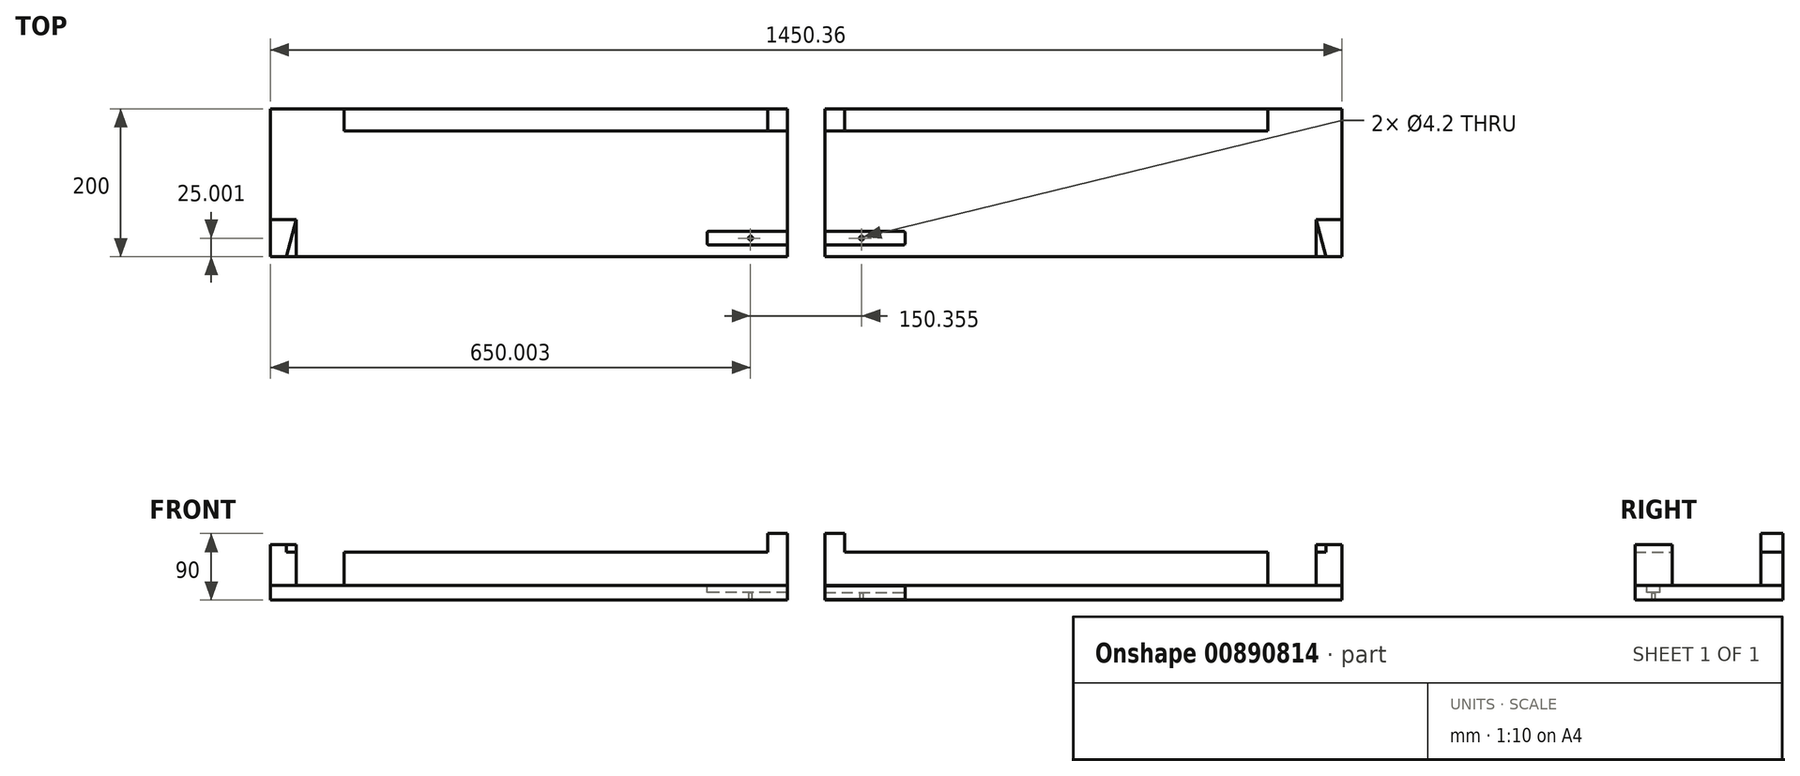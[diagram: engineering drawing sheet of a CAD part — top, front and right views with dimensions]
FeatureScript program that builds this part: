
annotation { "Feature Type Name" : "Feature", "Feature Type Description" : "" }
export const myFeature = defineFeature(function(context is Context, id is Id, definition is map)
    precondition{}
    {
        {
            var Q0;
            Q0=qCreatedBy(makeId("Top.planeOp"),FACE);
            var sketch = newSketch(context, id + "F0", { "sketchPlane" : qUnion([Q0])});
            skLineSegment(sketch, "E0.bottom", {"start": v(-675.18, 188.43) * mm, "end": v(54.82, 188.43) * mm});
            skLineSegment(sketch, "E0.top", {"start": v(-675.18, -11.57) * mm, "end": v(54.82, -11.57) * mm});
            skLineSegment(sketch, "E0.left", {"start": v(-675.18, 188.43) * mm, "end": v(-675.18, -11.57) * mm});
            skLineSegment(sketch, "E0.right", {"start": v(54.82, 188.43) * mm, "end": v(54.82, -11.57) * mm});
            skSolve(sketch);
        }
        {
            var Q0;
            Q0=makeQuery(id+"F0.imprint","IMPRINT",FACE,{"disambiguationData":[TD([[makeQuery(id+"F0.imprint","IMPRINT",EDGE,{"derivedFrom":sQuery(id+"F0.wireOp",EDGE,"E0.bottom")}),-1.0]])]});
            extrude(context, id + "F1", {"entities" : qUnion([Q0]), "depth" : 20 * mm, "offsetDistance" : 25 * mm});
        }
        {
            var Q0;
            Q0=makeQuery(id+"F1.opExtrude","CAP_FACE",FACE,{"disambiguationData":[OSD([sQuery(id+"F0.wireOp",EDGE,"E0.bottom"),sQuery(id+"F0.wireOp",EDGE,"E0.top"),sQuery(id+"F0.wireOp",EDGE,"E0.left"),sQuery(id+"F0.wireOp",EDGE,"E0.right")])],"isStart":false});
            var sketch = newSketch(context, id + "F2", { "sketchPlane" : qUnion([Q0])});
            skLineSegment(sketch, "E1.bottom", {"start": v(54.82, 188.43) * mm, "end": v(-545.18, 188.43) * mm});
            skLineSegment(sketch, "E1.top", {"start": v(54.82, 158.43) * mm, "end": v(-545.18, 158.43) * mm});
            skLineSegment(sketch, "E1.left", {"start": v(54.82, 188.43) * mm, "end": v(54.82, 158.43) * mm});
            skLineSegment(sketch, "E1.right", {"start": v(-545.18, 188.43) * mm, "end": v(-545.18, 158.43) * mm});
            skSolve(sketch);
        }
        {
            var Q0;
            Q0=makeQuery(id+"F2.imprint","IMPRINT",FACE,{"disambiguationData":[TD([[makeQuery(id+"F2.imprint","IMPRINT",EDGE,{"derivedFrom":sQuery(id+"F2.wireOp",EDGE,"E1.bottom")}),-1.0]])]});
            extrude(context, id + "F3", {"entities" : qUnion([Q0]), "depth" : 45 * mm, "offsetDistance" : 25 * mm});
        }
        {
            var Q0;
            Q0=makeQuery(id+"F3.opExtrude","CAP_FACE",FACE,{"disambiguationData":[OSD([sQuery(id+"F2.wireOp",EDGE,"E1.bottom"),sQuery(id+"F2.wireOp",EDGE,"E1.top"),sQuery(id+"F2.wireOp",EDGE,"E1.left"),sQuery(id+"F2.wireOp",EDGE,"E1.right")])],"isStart":false});
            var sketch = newSketch(context, id + "F4", { "sketchPlane" : qUnion([Q0])});
            skLineSegment(sketch, "E2.bottom", {"start": v(54.82, 188.43) * mm, "end": v(27.82, 188.43) * mm});
            skLineSegment(sketch, "E2.top", {"start": v(54.82, 158.43) * mm, "end": v(27.82, 158.43) * mm});
            skLineSegment(sketch, "E2.left", {"start": v(54.82, 188.43) * mm, "end": v(54.82, 158.43) * mm});
            skLineSegment(sketch, "E2.right", {"start": v(27.82, 188.43) * mm, "end": v(27.82, 158.43) * mm});
            skSolve(sketch);
        }
        {
            var Q0;
            Q0=makeQuery(id+"F4.imprint","IMPRINT",FACE,{"disambiguationData":[TD([[makeQuery(id+"F4.imprint","IMPRINT",EDGE,{"derivedFrom":sQuery(id+"F4.wireOp",EDGE,"E2.bottom")}),-1.0]])]});
            extrude(context, id + "F5", {"entities" : qUnion([Q0]), "operationType" : NewBodyOperationType.ADD, "depth" : 25 * mm, "offsetDistance" : 25 * mm});
        }
        {
            var Q0;
            Q0=makeQuery(id+"F1.opExtrude","CAP_FACE",FACE,{"disambiguationData":[OSD([sQuery(id+"F0.wireOp",EDGE,"E0.bottom"),sQuery(id+"F0.wireOp",EDGE,"E0.top"),sQuery(id+"F0.wireOp",EDGE,"E0.left"),sQuery(id+"F0.wireOp",EDGE,"E0.right")])],"isStart":false});
            var sketch = newSketch(context, id + "F6", { "sketchPlane" : qUnion([Q0])});
            skLineSegment(sketch, "E3.bottom", {"start": v(-665.18, -11.57) * mm, "end": v(-610.48, -11.57) * mm});
            skLineSegment(sketch, "E3.top", {"start": v(-665.18, 38.43) * mm, "end": v(-610.48, 38.43) * mm});
            skLineSegment(sketch, "E3.right", {"start": v(-610.48, -11.57) * mm, "end": v(-610.48, 38.43) * mm});
            skLineSegment(sketch, "E4.0", {"start": v(-665.18, -11.57) * mm, "end": v(-665.18, 38.43) * mm});
            skSolve(sketch);
        }
        {
            var Q0;
            Q0=makeQuery(id+"F6.imprint","IMPRINT",FACE,{"disambiguationData":[TD([[makeQuery(id+"F6.imprint","IMPRINT",EDGE,{"derivedFrom":sQuery(id+"F6.wireOp",EDGE,"E3.bottom")}),1.0]])]});
            extrude(context, id + "F7", {"entities" : qUnion([Q0]), "depth" : 45 * mm, "offsetDistance" : 25 * mm});
        }
        {
            var Q0;
            Q0=makeQuery(id+"F7.opExtrude","CAP_FACE",FACE,{"disambiguationData":[OSD([sQuery(id+"F6.wireOp",EDGE,"E3.bottom"),sQuery(id+"F6.wireOp",EDGE,"E3.top"),sQuery(id+"F6.wireOp",EDGE,"E3.left"),sQuery(id+"F6.wireOp",EDGE,"E3.right")])],"isStart":false});
            var sketch = newSketch(context, id + "F8", { "sketchPlane" : qUnion([Q0])});
            skLineSegment(sketch, "E5", {"start": v(-665.18, 38.43) * mm, "end": v(-610.48, 38.43) * mm});
            skLineSegment(sketch, "E6", {"start": v(-665.18, -11.57) * mm, "end": v(-665.18, 38.43) * mm});
            skLineSegment(sketch, "E7", {"start": v(-665.18, -11.57) * mm, "end": v(-623.58, -11.57) * mm});
            skLineSegment(sketch, "E8", {"start": v(-610.48, 38.43) * mm, "end": v(-623.58, -11.57) * mm});
            skSolve(sketch);
        }
        {
            var Q0;
            Q0=makeQuery(id+"F8.imprint","IMPRINT",FACE,{"disambiguationData":[TD([[makeQuery(id+"F8.imprint","IMPRINT",EDGE,{"derivedFrom":sQuery(id+"F8.wireOp",EDGE,"E5")}),-1.0]])]});
            extrude(context, id + "F9", {"entities" : qUnion([Q0]), "operationType" : NewBodyOperationType.ADD, "depth" : 10 * mm, "offsetDistance" : 25 * mm});
        }
        {
            var Q0;
            Q0=makeQuery(id+"F1.opExtrude","CAP_FACE",FACE,{"disambiguationData":[OSD([sQuery(id+"F0.wireOp",EDGE,"E0.bottom"),sQuery(id+"F0.wireOp",EDGE,"E0.top"),sQuery(id+"F0.wireOp",EDGE,"E0.left"),sQuery(id+"F0.wireOp",EDGE,"E0.right")])],"isStart":false});
            var sketch = newSketch(context, id + "F10", { "sketchPlane" : qUnion([Q0])});
            skLineSegment(sketch, "E9", {"start": v(54.82, 13.43) * mm, "end": v(-82.04, 13.43) * mm, "construction": true});
            skLineSegment(sketch, "E10.0", {"start": v(57.24, 22.43) * mm, "end": v(-52.18, 22.43) * mm});
            skLineSegment(sketch, "E11.0", {"start": v(57.24, 4.43) * mm, "end": v(-52.18, 4.43) * mm});
            skLineSegment(sketch, "E12", {"start": v(57.24, 22.43) * mm, "end": v(57.24, 4.43) * mm});
            skLineSegment(sketch, "E13", {"start": v(-54.18, 20.43) * mm, "end": v(-54.18, 6.43) * mm});
            skPoint(sketch, "E14.visualSharp", {"position": v(-54.18, 22.43) * mm});
            skArc(sketch, "E14.filletArc", {"start": v(-52.18, 22.43) * mm, "mid": v(-53.6, 21.84) * mm, "end": v(-54.18, 20.43) * mm});
            skPoint(sketch, "E15.visualSharp", {"position": v(-54.18, 4.43) * mm});
            skArc(sketch, "E15.filletArc", {"start": v(-54.18, 6.43) * mm, "mid": v(-53.6, 5.02) * mm, "end": v(-52.18, 4.43) * mm});
            skSolve(sketch);
        }
        {
            var Q0;
            Q0=makeQuery(id+"F10.imprint","IMPRINT",FACE,{"disambiguationData":[TD([[makeQuery(id+"F10.imprint","IMPRINT",EDGE,{"derivedFrom":sQuery(id+"F10.wireOp",EDGE,"E13")}),1.0]])]});
            extrude(context, id + "F11", {"entities" : qUnion([Q0]), "operationType" : NewBodyOperationType.REMOVE, "oppositeDirection" : true, "depth" : 10 * mm, "offsetDistance" : 25 * mm});
        }
        {
            var Q0;
            Q0=makeQuery(id+"F11.boolean.opBoolean","COPY",FACE,{"derivedFrom":makeQuery(id+"F11.opExtrude","CAP_FACE",FACE,{"disambiguationData":[OSD([sQuery(id+"F0.wireOp",EDGE,"E0.right"),sQuery(id+"F10.wireOp",EDGE,"E10.0"),sQuery(id+"F10.wireOp",EDGE,"E11.0"),sQuery(id+"F10.wireOp",EDGE,"E13"),sQuery(id+"F10.wireOp",EDGE,"E14.filletArc"),sQuery(id+"F10.wireOp",EDGE,"E15.filletArc")])],"isStart":false})});
            var sketch = newSketch(context, id + "F12", { "sketchPlane" : qUnion([Q0])});
            skLineSegment(sketch, "E16", {"start": v(-59.39, 13.43) * mm, "end": v(59.1, 13.43) * mm, "construction": true});
            skLineSegment(sketch, "E17", {"start": v(4.82, 22.43) * mm, "end": v(4.82, 4.43) * mm, "construction": true});
            skPoint(sketch, "E18", {"position": v(4.82, 13.43) * mm});
            skSolve(sketch);
        }
        {
            var Q0;
            Q0=sQuery(id+"F12.wireOp",VERTEX,"E18");
            var Q1;
            Q1=makeQuery(id+"F1.opExtrude","SWEPT_BODY",BODY,{"disambiguationData":[OSD([sQuery(id+"F0.wireOp",EDGE,"E0.bottom"),sQuery(id+"F0.wireOp",EDGE,"E0.top"),sQuery(id+"F0.wireOp",EDGE,"E0.left"),sQuery(id+"F0.wireOp",EDGE,"E0.right")])]});
            hole(context, id + "F13", {"style" : HoleStyle.C_SINK, "endStyle" : HoleEndStyle.THROUGH, "holeDiameter" : 4.2 * mm, "cSinkDiameter" : 5.5 * mm, "cSinkAngle" : 90 * degree, "majorDiameter" : 5 * mm, "isTappedThrough" : true, "tappedDepth" : 12 * mm, "tapClearance" : 3, "locations" : qUnion([Q0]), "scope" : qUnion([Q1])});
        }
        {
            var Q0;
            Q0=makeQuery(id+"F9.opExtrude","CAP_FACE",FACE,{"disambiguationData":[OSD([sQuery(id+"F8.wireOp",EDGE,"E5"),sQuery(id+"F8.wireOp",EDGE,"E6"),sQuery(id+"F8.wireOp",EDGE,"E7"),sQuery(id+"F8.wireOp",EDGE,"E8")])],"isStart":false});
            var sketch = newSketch(context, id + "F14", { "sketchPlane" : qUnion([Q0])});
            skLineSegment(sketch, "E19.bottom", {"start": v(-700.3, 305.62) * mm, "end": v(-645.18, 305.62) * mm});
            skLineSegment(sketch, "E19.top", {"start": v(-700.3, -131.43) * mm, "end": v(-645.18, -131.43) * mm});
            skLineSegment(sketch, "E19.left", {"start": v(-700.3, 305.62) * mm, "end": v(-700.3, -131.43) * mm});
            skLineSegment(sketch, "E19.right", {"start": v(-645.18, 305.62) * mm, "end": v(-645.18, -131.43) * mm});
            skSolve(sketch);
        }
        {
            var Q0;
            {var subQ1=sQuery(id+"F14.wireOp",EDGE,"E19.bottom");Q0=makeQuery(id+"F14.imprint","IMPRINT",FACE,{"disambiguationData":[TD([[makeQuery(id+"F14.imprint","IMPRINT",EDGE,{"derivedFrom":subQ1}),-1.0]])]});}
            var Q1;
            {var subQ5=makeQuery(id+"F9.opExtrude","CAP_EDGE",EDGE,{"disambiguationData":[OSD([sQuery(id+"F8.wireOp",EDGE,"E6")])],"isStart":false});Q1=makeQuery(id+"F14.imprint","IMPRINT",FACE,{"disambiguationData":[TD([[makeQuery(id+"F14.imprint","IMPRINT",EDGE,{"derivedFrom":subQ5}),-1.0]])]});}
            extrude(context, id + "F15", {"entities" : qUnion([Q0, Q1]), "operationType" : NewBodyOperationType.REMOVE, "endBound" : BoundingType.THROUGH_ALL, "oppositeDirection" : true, "depth" : 25 * mm, "offsetDistance" : 25 * mm});
        }
        {
            var Q0;
            Q0=qCreatedBy(makeId("Right.planeOp"),FACE);
            cPlane(context, id + "F16", {"entities" : qUnion([Q0]), "cplaneType" : CPlaneType.OFFSET, "offset" : 80 * mm, "width" : 150 * mm, "height" : 150 * mm});
        }
        {
            var Q0;
            Q0=makeQuery(id+"F1.opExtrude","SWEPT_BODY",BODY,{"disambiguationData":[OSD([sQuery(id+"F0.wireOp",EDGE,"E0.bottom"),sQuery(id+"F0.wireOp",EDGE,"E0.top"),sQuery(id+"F0.wireOp",EDGE,"E0.left"),sQuery(id+"F0.wireOp",EDGE,"E0.right")])]});
            var Q1;
            Q1=makeQuery(id+"F3.opExtrude","SWEPT_BODY",BODY,{"disambiguationData":[OSD([sQuery(id+"F2.wireOp",EDGE,"E1.bottom"),sQuery(id+"F2.wireOp",EDGE,"E1.top"),sQuery(id+"F2.wireOp",EDGE,"E1.left"),sQuery(id+"F2.wireOp",EDGE,"E1.right")])]});
            var Q2;
            Q2=makeQuery(id+"F7.opExtrude","SWEPT_BODY",BODY,{"disambiguationData":[OSD([sQuery(id+"F6.wireOp",EDGE,"E3.bottom"),sQuery(id+"F6.wireOp",EDGE,"E3.top"),sQuery(id+"F6.wireOp",EDGE,"E3.right"),sQuery(id+"F6.wireOp",EDGE,"E4.0")])]});
            var Q3;
            Q3=qCreatedBy(id+"F16.planeOp",FACE);
            mirror(context, id + "F17", {"entities" : qUnion([Q0, Q1, Q2]), "mirrorPlane" : qUnion([Q3])});
        }
        {
            var Q0;
            Q0=makeQuery(id+"F17.opPattern","COPY",FACE,{"derivedFrom":makeQuery(id+"F1.opExtrude","SWEPT_FACE",FACE,{"disambiguationData":[OSD([sQuery(id+"F0.wireOp",EDGE,"E0.top")])]}),"instanceName":"1"});
            var sketch = newSketch(context, id + "F18", { "sketchPlane" : qUnion([Q0])});
            skLineSegment(sketch, "E20.bottom", {"start": v(105.18, 19) * mm, "end": v(214.18, 19) * mm});
            skLineSegment(sketch, "E20.top", {"start": v(105.18, 1) * mm, "end": v(214.18, 1) * mm});
            skLineSegment(sketch, "E20.left", {"start": v(105.18, 19) * mm, "end": v(105.18, 1) * mm});
            skLineSegment(sketch, "E20.right", {"start": v(214.18, 19) * mm, "end": v(214.18, 1) * mm});
            skSolve(sketch);
        }
        {
            var Q0;
            Q0=makeQuery(id+"F18.imprint","IMPRINT",FACE,{"disambiguationData":[TD([[makeQuery(id+"F18.imprint","IMPRINT",EDGE,{"derivedFrom":sQuery(id+"F18.wireOp",EDGE,"E20.bottom")}),-1.0]])]});
            extrude(context, id + "F19", {"entities" : qUnion([Q0]), "operationType" : NewBodyOperationType.REMOVE, "oppositeDirection" : true, "depth" : 1 * mm, "offsetDistance" : 25 * mm});
        }
    });
